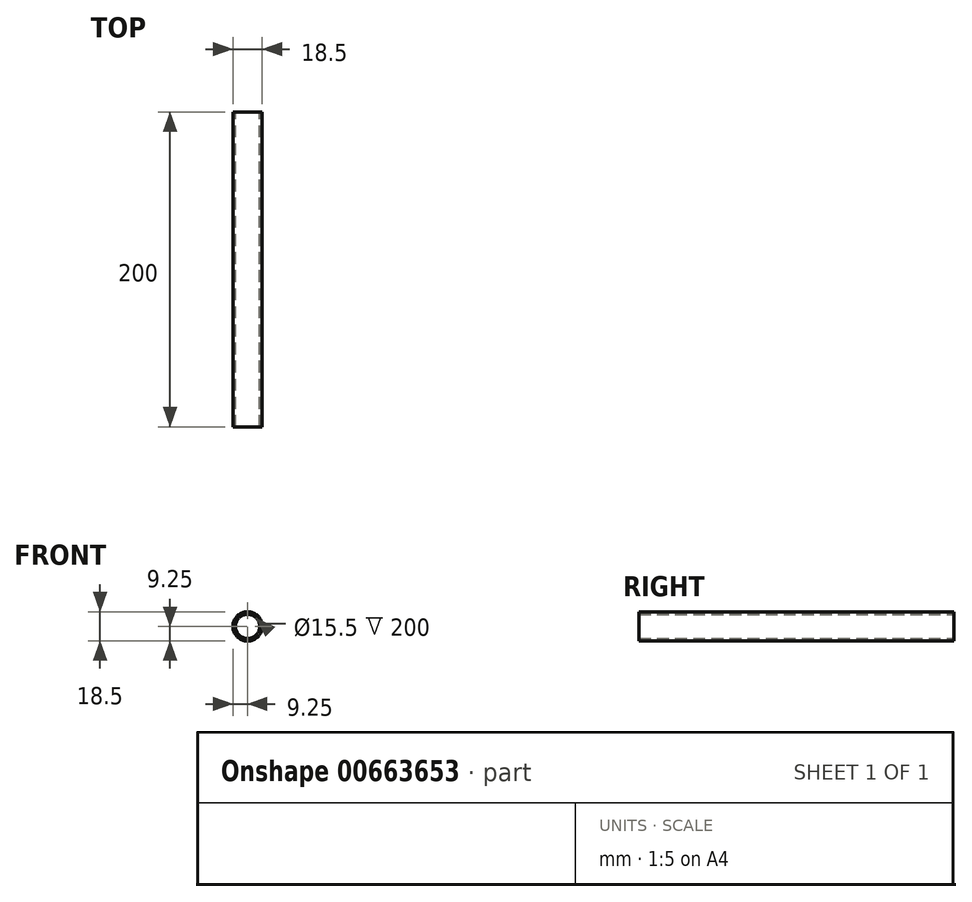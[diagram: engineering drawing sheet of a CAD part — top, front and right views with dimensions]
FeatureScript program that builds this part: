
annotation { "Feature Type Name" : "Feature", "Feature Type Description" : "" }
export const myFeature = defineFeature(function(context is Context, id is Id, definition is map)
    precondition{}
    {
        {
            var Q0;
            Q0=qCreatedBy(makeId("Front.planeOp"),FACE);
            var sketch = newSketch(context, id + "F0", { "sketchPlane" : qUnion([Q0])});
            skCircle(sketch, "E0", {"center": v(0, 0) * mm, "radius": 9.25 * mm});
            skCircle(sketch, "E1.0", {"center": v(0, 0) * mm, "radius": 7.75 * mm});
            skSolve(sketch);
        }
        {
            var Q0;
            Q0 = qSketchRegion(id + "F0", true);
            extrude(context, id + "F1", {"entities" : qUnion([Q0]), "depth" : 200 * mm, "offsetDistance" : 25 * mm});
        }
    });
